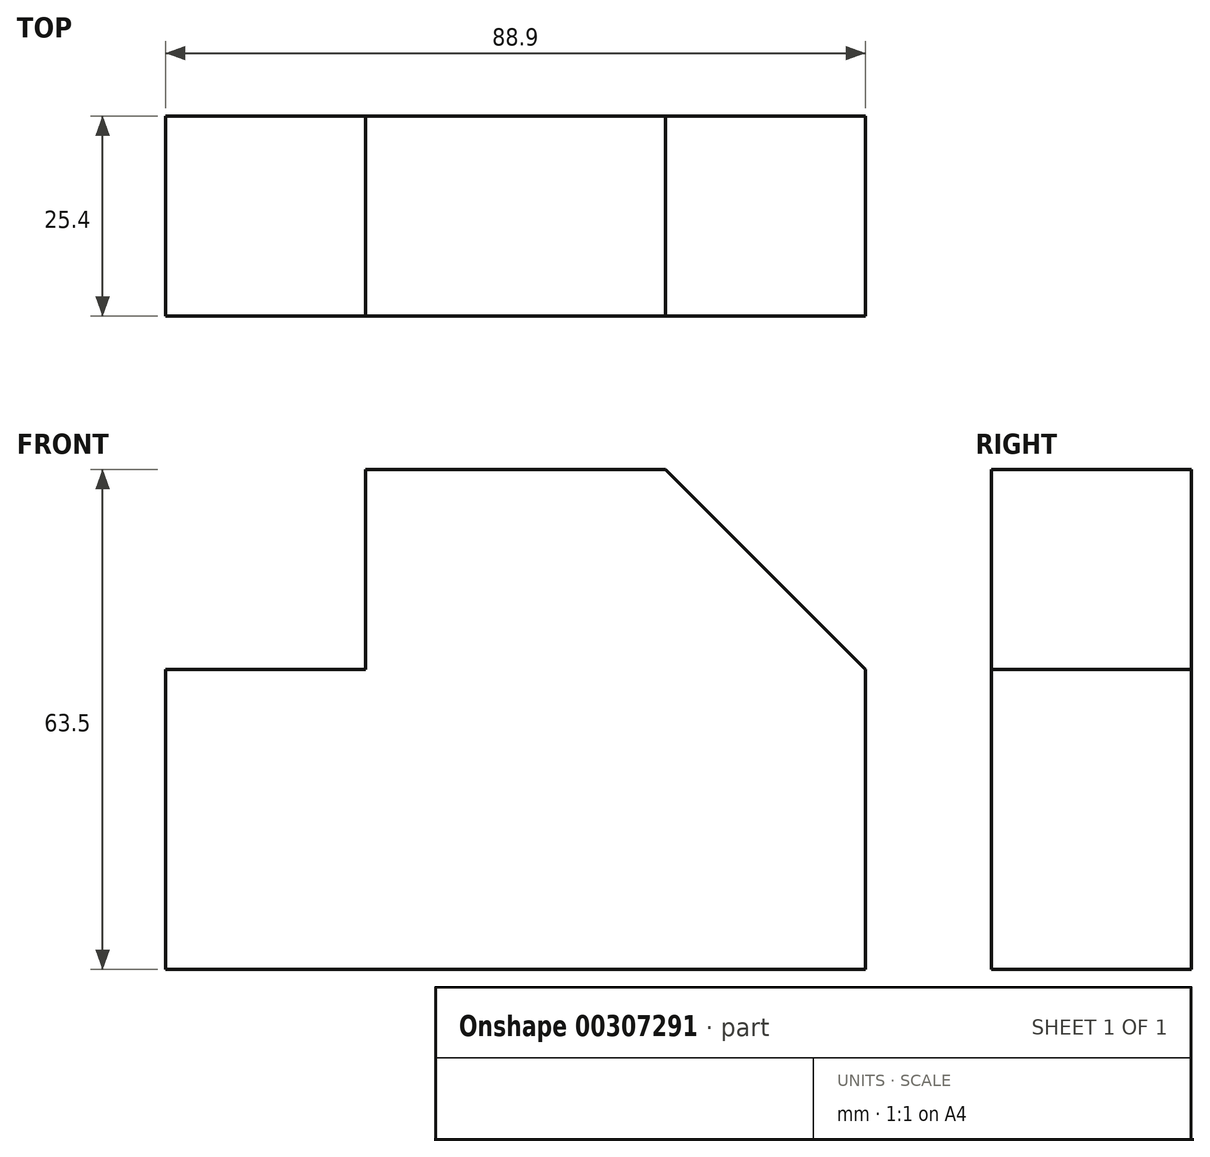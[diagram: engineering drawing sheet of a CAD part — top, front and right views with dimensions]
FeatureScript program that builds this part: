
annotation { "Feature Type Name" : "Feature", "Feature Type Description" : "" }
export const myFeature = defineFeature(function(context is Context, id is Id, definition is map)
    precondition{}
    {
        {
            var Q0;
            Q0=qCreatedBy(makeId("Front.planeOp"),FACE);
            var sketch = newSketch(context, id + "F0", { "sketchPlane" : qUnion([Q0])});
            skLineSegment(sketch, "E0", {"start": v(-42, -42.1) * mm, "end": v(46.9, -42.1) * mm});
            skLineSegment(sketch, "E1", {"start": v(-42, -42.1) * mm, "end": v(-42, -4) * mm});
            skLineSegment(sketch, "E2", {"start": v(-42, -4) * mm, "end": v(-16.6, -4) * mm});
            skLineSegment(sketch, "E3", {"start": v(-16.6, -4) * mm, "end": v(-16.6, 21.4) * mm});
            skLineSegment(sketch, "E4", {"start": v(-16.6, 21.4) * mm, "end": v(21.5, 21.4) * mm});
            skLineSegment(sketch, "E5", {"start": v(46.9, -42.1) * mm, "end": v(46.9, -4) * mm});
            skLineSegment(sketch, "E6", {"start": v(21.5, 21.4) * mm, "end": v(46.9, -4) * mm});
            skSolve(sketch);
        }
        {
            var Q0;
            Q0=makeQuery(id+"F0.imprint","IMPRINT",FACE,{"disambiguationData":[TD([[makeQuery(id+"F0.imprint","IMPRINT",EDGE,{"derivedFrom":sQuery(id+"F0.wireOp",EDGE,"E0")}),1.0]])]});
            extrude(context, id + "F1", {"entities" : qUnion([Q0]), "depth" : 25.4 * mm});
        }
    });
